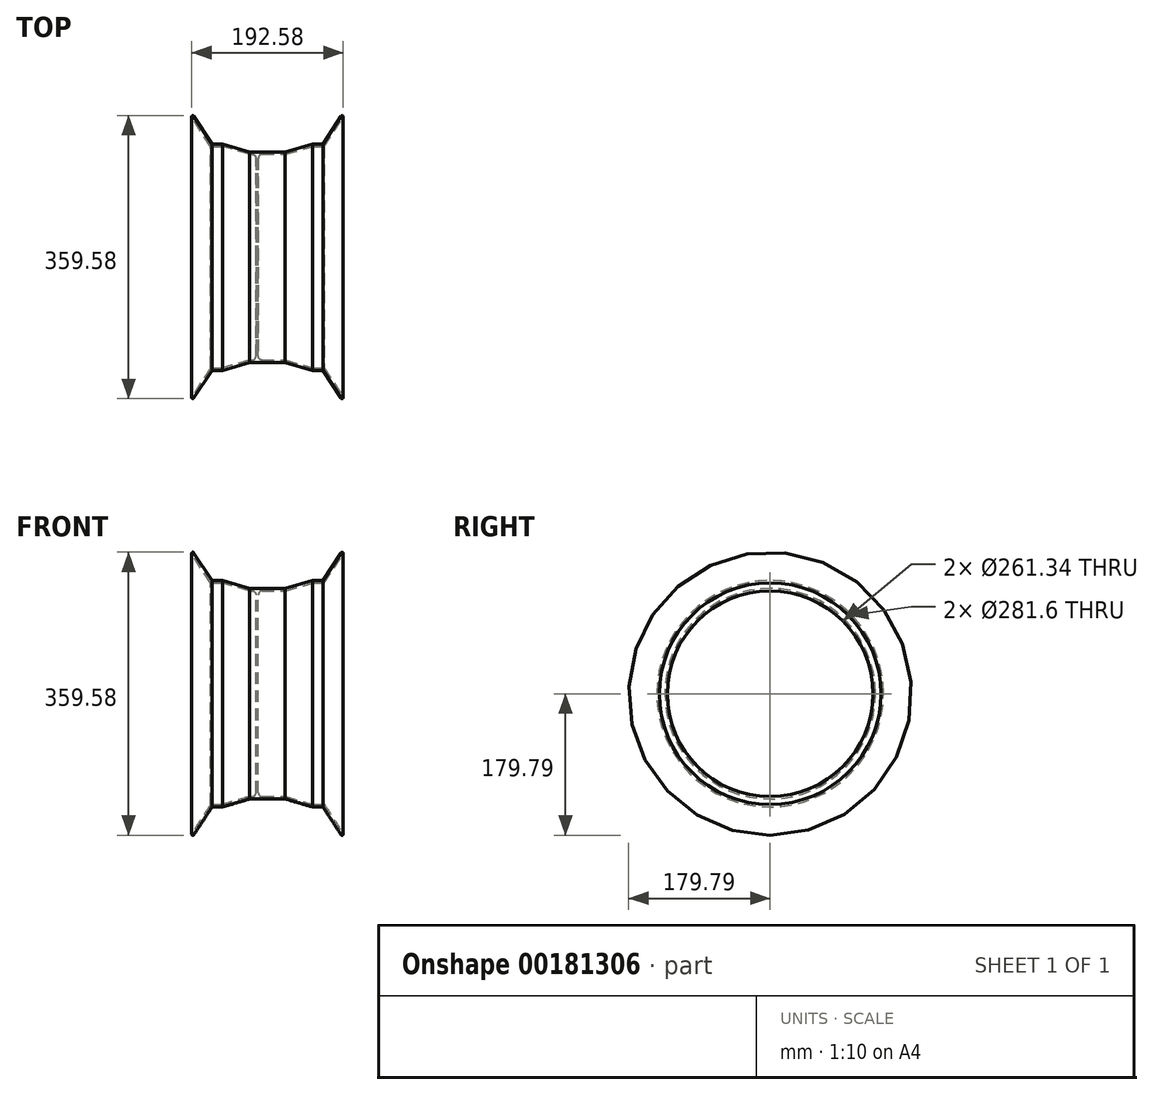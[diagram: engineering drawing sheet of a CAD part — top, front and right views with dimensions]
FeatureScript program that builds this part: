
annotation { "Feature Type Name" : "Feature", "Feature Type Description" : "" }
export const myFeature = defineFeature(function(context is Context, id is Id, definition is map)
    precondition{}
    {
        {
            var Q0;
            Q0=qCreatedBy(makeId("Front.planeOp"),FACE);
            var sketch = newSketch(context, id + "F0", { "sketchPlane" : qUnion([Q0])});
            skLineSegment(sketch, "E0", {"start": v(57.3, -34) * mm, "end": v(70.47, -34) * mm});
            skLineSegment(sketch, "E1", {"start": v(0, -44.13) * mm, "end": v(22.62, -44.13) * mm});
            skLineSegment(sketch, "E2", {"start": v(22.62, -44.13) * mm, "end": v(57.3, -34) * mm});
            skLineSegment(sketch, "E3", {"start": v(70.47, -34) * mm, "end": v(93.54, 1.3) * mm});
            skLineSegment(sketch, "E4.MirrorCS", {"start": v(0, -44.13) * mm, "end": v(-22.62, -44.13) * mm});
            skLineSegment(sketch, "E5.MirrorCS", {"start": v(-22.62, -44.13) * mm, "end": v(-57.3, -34) * mm});
            skLineSegment(sketch, "E6.MirrorCS", {"start": v(-57.3, -34) * mm, "end": v(-70.47, -34) * mm});
            skLineSegment(sketch, "E7.MirrorCS", {"start": v(-70.47, -34) * mm, "end": v(-93.54, 1.3) * mm});
            skLineSegment(sketch, "E8.0", {"start": v(0, -177.8) * mm, "end": v(-118.2, -177.8) * mm});
            skPoint(sketch, "E9.7.internal.orphan", {"position": v(56.65, 129.5) * mm});
            skPoint(sketch, "E10.start.orphan", {"position": v(0, 129.5) * mm});
            skPoint(sketch, "E11.MirrorCS.end.orphan", {"position": v(-56.65, 129.5) * mm});
            skLineSegment(sketch, "E12.0", {"start": v(-72.1, -37) * mm, "end": v(-96.05, -0.33) * mm});
            skLineSegment(sketch, "E12.1", {"start": v(-57.74, -37) * mm, "end": v(-72.1, -37) * mm});
            skLineSegment(sketch, "E12.2", {"start": v(-23.05, -47.13) * mm, "end": v(-57.74, -37) * mm});
            skLineSegment(sketch, "E12.3", {"start": v(0, -47.13) * mm, "end": v(-6.66, -47.13) * mm});
            skArc(sketch, "E13", {"start": v(-93.54, 1.3) * mm, "mid": v(-95.61, 1.74) * mm, "end": v(-96.05, -0.33) * mm});
            skArc(sketch, "E14.MirrorCS", {"start": v(93.54, 1.3) * mm, "mid": v(95.61, 1.74) * mm, "end": v(96.05, -0.33) * mm});
            skLineSegment(sketch, "E15.MirrorCS", {"start": v(72.1, -37) * mm, "end": v(96.05, -0.33) * mm});
            skLineSegment(sketch, "E16.MirrorCS", {"start": v(57.74, -37) * mm, "end": v(72.1, -37) * mm});
            skLineSegment(sketch, "E17.MirrorCS", {"start": v(23.05, -47.13) * mm, "end": v(57.74, -37) * mm});
            skLineSegment(sketch, "E18.MirrorCS", {"start": v(0, -47.13) * mm, "end": v(23.05, -47.13) * mm});
            skLineSegment(sketch, "E19", {"start": v(-14.66, -52.13) * mm, "end": v(-14.66, -177.8) * mm});
            skLineSegment(sketch, "E20.0", {"start": v(-11.66, -52.13) * mm, "end": v(-11.66, -177.8) * mm});
            skLineSegment(sketch, "E21.trimOffspring", {"start": v(-19.66, -47.13) * mm, "end": v(-23.05, -47.13) * mm});
            skPoint(sketch, "E22.visualSharp", {"position": v(-14.66, -47.13) * mm});
            skArc(sketch, "E22.filletArc", {"start": v(-14.66, -52.13) * mm, "mid": v(-16.13, -48.6) * mm, "end": v(-19.66, -47.13) * mm});
            skPoint(sketch, "E23.visualSharp", {"position": v(-11.66, -47.13) * mm});
            skArc(sketch, "E23.filletArc", {"start": v(-6.66, -47.13) * mm, "mid": v(-10.2, -48.6) * mm, "end": v(-11.66, -52.13) * mm});
            skSolve(sketch);
        }
        {
            var Q0;
            Q0=qSketchRegion(id+"F0",true);
            var Q1;
            Q1=sQuery(id+"F0.wireOp",EDGE,"E8.0");
            revolve(context, id + "F1", {"entities" : qUnion([Q0]), "axis" : qUnion([Q1]), "revolveType" : RevolveType.FULL});
        }
    });
